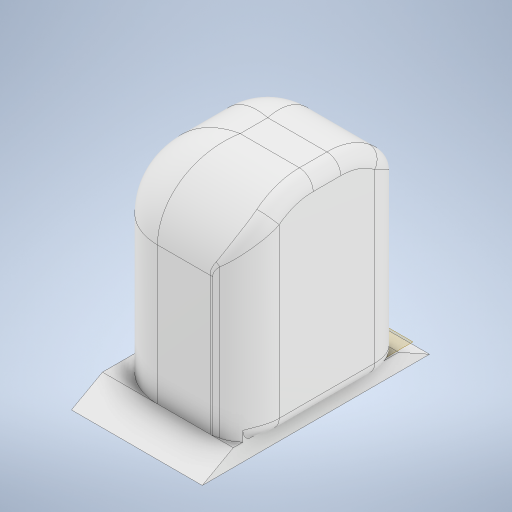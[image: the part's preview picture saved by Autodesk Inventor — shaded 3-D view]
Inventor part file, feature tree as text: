
AUTODESK INVENTOR PART (.ipt)
format: ipt  version: 2024 (Build 280153000, 153)  size: 396,800 bytes
history: native  units: mm
features: fillet x3, sketch x2, extrude x2, plane x1, loft x1
ambient origin geometry x8: Origin, YZ Plane, XZ Plane, XY Plane, X Axis, Y Axis, Z Axis, Center Point
bodies: Solid1 (feature_tree)
feature tree (9):
  plane  "Work Plane1"
  sketch  "Sketch3"  dims[d0=19.0mm d1=33.0mm]
  loft  "base"
  extrude  "finger_extrusion"  TaperAngle=0.0deg  [1 undecoded]
  fillet  "Fillet1"  Radius=19.0mm
  fillet  "Fillet2"  Radius=24.0mm
  fillet  "Fillet3"  Radius=4.5mm
  extrude  "brass_insert_holes"  TaperAngle=0.0deg  [1 undecoded]
  sketch  "Sketch12"  dims[d26=2.5mm d27=0.0mm d28=0.0mm d29=19.0mm d30=24.0mm d31=4.5mm d32=19.0mm d33=33.0mm d34=2.5mm d35=2.5mm d36=2.5mm d37=2.5mm d38=2.5mm d39=2.5mm d40=3.5mm d41=3.5mm d42=16.5mm d43=16.5mm d44=7.5mm d45=7.5mm d46=7.5mm d47=7.5mm d48=6.5mm d49=6.5mm d50=6.5mm d51=6.5mm d52=0.0mm d53=0.0mm d54=0.0mm d55=90.0deg d56=0.0mm d57=90.0deg d58=20.0mm d59=0.0mm d105=90.0deg d106=12.0mm d107=90.0deg d108=5.0mm d109=8.0mm d110=8.0mm d111=30.0mm d112=0.0mm d113=10.0mm d114=2.0mm d115=2.0mm d66=0.5mm d67=0.872665mm d68=0.5mm d69=0.872665mm]
note: 2 required parameter values undecoded (feature->parameter linkage not recoverable at this tier; creation-order binding heuristic only, values carry confidence <= 0.55)
